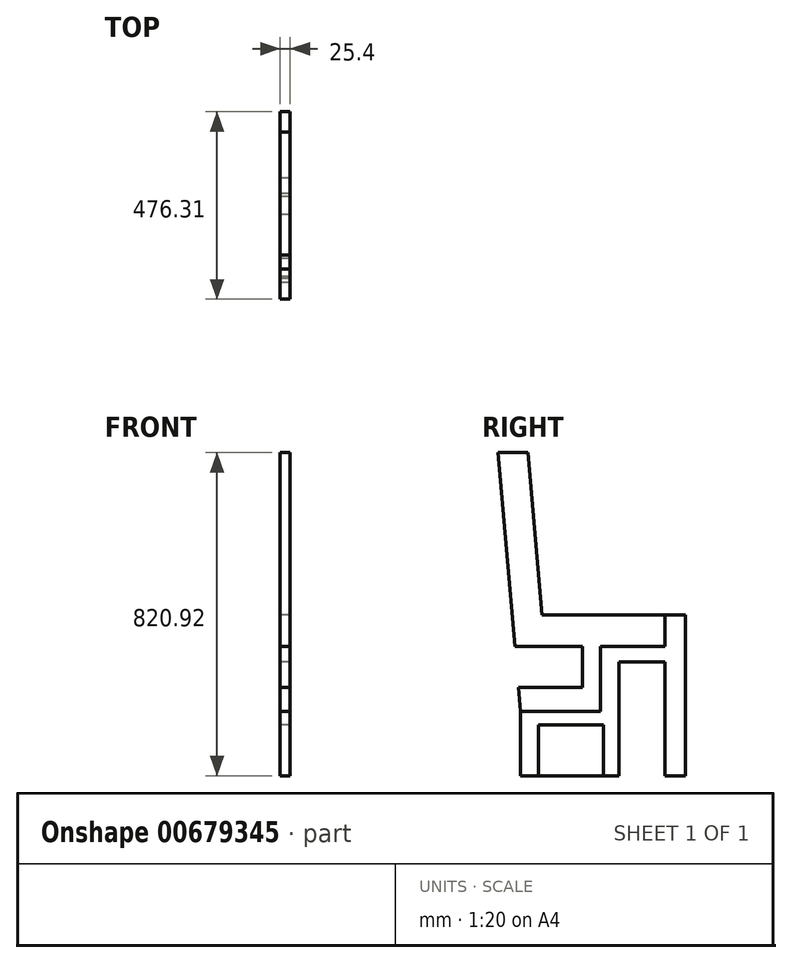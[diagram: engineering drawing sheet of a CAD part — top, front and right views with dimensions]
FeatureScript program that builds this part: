
annotation { "Feature Type Name" : "Feature", "Feature Type Description" : "" }
export const myFeature = defineFeature(function(context is Context, id is Id, definition is map)
    precondition{}
    {
        {
            var Q0;
            Q0=qCreatedBy(makeId("Right.planeOp"),FACE);
            var sketch = newSketch(context, id + "F0", { "sketchPlane" : qUnion([Q0])});
            skLineSegment(sketch, "E0", {"start": v(0.44, -2.35) * mm, "end": v(0.44, 162.75) * mm});
            skLineSegment(sketch, "E1", {"start": v(203.64, 162.75) * mm, "end": v(0.44, 162.75) * mm});
            skLineSegment(sketch, "E2", {"start": v(203.64, 162.75) * mm, "end": v(203.64, 327.85) * mm});
            skLineSegment(sketch, "E3", {"start": v(188.63, 327.85) * mm, "end": v(367.45, 327.85) * mm});
            skLineSegment(sketch, "E4", {"start": v(612.73, 408.06) * mm, "end": v(612.73, 0) * mm, "construction": true});
            skLineSegment(sketch, "E5", {"start": v(14.39, 162.75) * mm, "end": v(-951.19, 162.75) * mm, "construction": true});
            skLineSegment(sketch, "E6", {"start": v(406.4, 0) * mm, "end": v(-5.65, -0.28) * mm});
            skLineSegment(sketch, "E7", {"start": v(612.73, 0) * mm, "end": v(406.4, 0) * mm, "construction": true});
            skLineSegment(sketch, "E8", {"start": v(419.19, 408.06) * mm, "end": v(55.18, 408.06) * mm});
            skLineSegment(sketch, "E9", {"start": v(-21.15, 409.46) * mm, "end": v(0.44, 162.75) * mm});
            skLineSegment(sketch, "E10", {"start": v(419.19, 408.06) * mm, "end": v(612.73, 408.06) * mm, "construction": true});
            skLineSegment(sketch, "E11", {"start": v(-21.15, 409.46) * mm, "end": v(-57.12, 820.64) * mm});
            skLineSegment(sketch, "E12", {"start": v(-26.1, 162.75) * mm, "end": v(14.39, 162.75) * mm});
            skLineSegment(sketch, "E13", {"start": v(400.75, 0) * mm, "end": v(419.19, 0) * mm});
            skLineSegment(sketch, "E14", {"start": v(19.09, 820.64) * mm, "end": v(55.18, 408.06) * mm});
            skLineSegment(sketch, "E15", {"start": v(419.19, 408.06) * mm, "end": v(419.19, 0) * mm});
            skLineSegment(sketch, "E16.top", {"start": v(46.13, 224.39) * mm, "end": v(157.66, 224.39) * mm});
            skLineSegment(sketch, "E16.right", {"start": v(157.66, 224.39) * mm, "end": v(157.66, 328.78) * mm});
            skLineSegment(sketch, "E17.top", {"start": v(250.8, 288.85) * mm, "end": v(367.45, 288.85) * mm});
            skLineSegment(sketch, "E17.left", {"start": v(250.8, -4.98) * mm, "end": v(250.8, 288.85) * mm});
            skLineSegment(sketch, "E18.bottom", {"start": v(46.76, -0.25) * mm, "end": v(211.3, -0.25) * mm});
            skLineSegment(sketch, "E18.top", {"start": v(46.76, 128.62) * mm, "end": v(211.3, 128.62) * mm});
            skLineSegment(sketch, "E18.left", {"start": v(46.76, -0.25) * mm, "end": v(46.76, 128.62) * mm});
            skLineSegment(sketch, "E18.right", {"start": v(211.3, -0.25) * mm, "end": v(211.3, 128.62) * mm});
            skLineSegment(sketch, "E19", {"start": v(367.45, 327.85) * mm, "end": v(367.45, 414.2) * mm});
            skLineSegment(sketch, "E20", {"start": v(-57.12, 820.64) * mm, "end": v(19.09, 820.64) * mm});
            skLineSegment(sketch, "E21", {"start": v(367.45, 327.85) * mm, "end": v(419.19, 328.24) * mm});
            skLineSegment(sketch, "E22", {"start": v(419.19, 328.24) * mm, "end": v(419.19, -110.49) * mm});
            skLineSegment(sketch, "E23", {"start": v(367.45, 327.85) * mm, "end": v(367.45, -70.12) * mm});
            skLineSegment(sketch, "E24", {"start": v(211.3, 128.62) * mm, "end": v(250.8, 128.62) * mm});
            skLineSegment(sketch, "E25", {"start": v(46.13, 224.39) * mm, "end": v(32.73, 377.58) * mm});
            skLineSegment(sketch, "E26", {"start": v(157.66, 356.28) * mm, "end": v(157.66, 224.39) * mm});
            skLineSegment(sketch, "E27", {"start": v(33.9, 29.15) * mm, "end": v(367.45, 29.15) * mm});
            skLineSegment(sketch, "E28", {"start": v(157.66, 328.78) * mm, "end": v(-36.96, 328.78) * mm});
            skLineSegment(sketch, "E29", {"start": v(46.13, 224.39) * mm, "end": v(-43.71, 224.39) * mm});
            skSolve(sketch);
        }
        {
            var Q0;
            {var subQ0=sQuery(id+"F0.wireOp",EDGE,"E11");Q0=makeQuery(id+"F0.imprint","IMPRINT",FACE,{"disambiguationData":[TD([[makeQuery(id+"F0.imprint","IMPRINT",EDGE,{"derivedFrom":subQ0}),-1.0]])]});}
            var Q1;
            Q1=makeQuery(id+"F0.imprint","IMPRINT",FACE,{"disambiguationData":[TD([[makeQuery(id+"F0.imprint","IMPRINT",EDGE,{"derivedFrom":sQuery(id+"F0.wireOp",EDGE,"E1")}),-1.0]])]});
            var Q2;
            {var subQ0=sQuery(id+"F0.wireOp",EDGE,"E19");var subQ5=sQuery(id+"F0.wireOp",EDGE,"E8");var subQ6=makeQuery(id+"F0.imprint","INTERSECT",VERTEX,{"derivedFrom":[subQ5,subQ0]});Q2=makeQuery(id+"F0.imprint","IMPRINT",FACE,{"disambiguationData":[TD([[makeQuery(id+"F0.imprint","IMPRINT",EDGE,{"disambiguationData":[TD([[subQ6,-1.0]])],"derivedFrom":subQ5}),1.0]])]});}
            var Q3;
            {var subQ0=sQuery(id+"F0.wireOp",EDGE,"UJc8SRw5-JCp4-3w58-zdoM-WuLl9uJl6UIW");Q3=makeQuery(id+"F0.imprint","IMPRINT",FACE,{"disambiguationData":[TD([[makeQuery(id+"F0.imprint","IMPRINT",EDGE,{"derivedFrom":subQ0}),-1.0]])]});}
            var Q4;
            {var subQ0=sQuery(id+"F0.wireOp",EDGE,"a74wy1ss-w96l-n5P1-hgLf-OixQSZHb7zzw");Q4=makeQuery(id+"F0.imprint","IMPRINT",FACE,{"disambiguationData":[TD([[makeQuery(id+"F0.imprint","IMPRINT",EDGE,{"derivedFrom":subQ0}),1.0]])]});}
            extrude(context, id + "F1", {"entities" : qUnion([Q0, Q1, Q2, Q3, Q4]), "depth" : 25.4 * mm, "offsetDistance" : 25.4 * mm});
        }
        {
            var Q0;
            {var subQ0=sQuery(id+"F0.wireOp",EDGE,"E17.top");var subQ1=sQuery(id+"F0.wireOp",EDGE,"oAci7Kaw-5Hkm-9jKa-Rgxa-tkB4P00vJvvU");var subQ2=makeQuery(id+"F0.imprint","INTERSECT",VERTEX,{"derivedFrom":[subQ1,subQ0]});Q0=makeQuery(id+"F0.imprint","IMPRINT",FACE,{"disambiguationData":[TD([[makeQuery(id+"F0.imprint","IMPRINT",EDGE,{"disambiguationData":[TD([[subQ2,-1.0]])],"derivedFrom":subQ1}),-1.0]])]});}
            var Q1;
            {var subQ0=sQuery(id+"F0.wireOp",EDGE,"oAci7Kaw-5Hkm-9jKa-Rgxa-tkB4P00vJvvU");var subQ5=sQuery(id+"F0.wireOp",EDGE,"E17.top");var subQ7=makeQuery(id+"F0.imprint","INTERSECT",VERTEX,{"derivedFrom":[subQ0,subQ5]});Q1=makeQuery(id+"F0.imprint","IMPRINT",FACE,{"disambiguationData":[TD([[makeQuery(id+"F0.imprint","IMPRINT",EDGE,{"disambiguationData":[TD([[subQ7,1.0]])],"derivedFrom":subQ5}),1.0]])]});}
            var Q2;
            {var subQ1=sQuery(id+"F0.wireOp",EDGE,"E8");var subQ3=sQuery(id+"F0.wireOp",EDGE,"E19");var subQ4=makeQuery(id+"F0.imprint","INTERSECT",VERTEX,{"derivedFrom":[subQ1,subQ3]});Q2=makeQuery(id+"F0.imprint","IMPRINT",FACE,{"disambiguationData":[TD([[makeQuery(id+"F0.imprint","IMPRINT",EDGE,{"disambiguationData":[TD([[subQ4,1.0]])],"derivedFrom":subQ1}),1.0]])]});}
            var Q3;
            {var subQ1=sQuery(id+"F0.wireOp",EDGE,"E15");var subQ3=sQuery(id+"F0.wireOp",EDGE,"E21");var subQ4=makeQuery(id+"F0.imprint","INTERSECT",VERTEX,{"derivedFrom":[subQ1,subQ3]});Q3=makeQuery(id+"F0.imprint","IMPRINT",FACE,{"disambiguationData":[TD([[makeQuery(id+"F0.imprint","IMPRINT",EDGE,{"disambiguationData":[TD([[subQ4,1.0]])],"derivedFrom":subQ3}),1.0]])]});}
            var Q4;
            {var subQ1=sQuery(id+"F0.wireOp",EDGE,"E21");Q4=makeQuery(id+"F0.imprint","IMPRINT",FACE,{"disambiguationData":[TD([[makeQuery(id+"F0.imprint","IMPRINT",EDGE,{"derivedFrom":subQ1}),-1.0]])]});}
            var Q5;
            {var subQ0=sQuery(id+"F0.wireOp",EDGE,"E18.bottom");Q5=makeQuery(id+"F0.imprint","IMPRINT",FACE,{"disambiguationData":[TD([[makeQuery(id+"F0.imprint","IMPRINT",EDGE,{"derivedFrom":subQ0}),1.0]])]});}
            var Q6;
            {var subQ0=sQuery(id+"F0.wireOp",EDGE,"E24");Q6=makeQuery(id+"F0.imprint","IMPRINT",FACE,{"disambiguationData":[TD([[makeQuery(id+"F0.imprint","IMPRINT",EDGE,{"derivedFrom":subQ0}),-1.0]])]});}
            var Q7;
            {var subQ0=sQuery(id+"F0.wireOp",EDGE,"E17.left");var subQ1=sQuery(id+"F0.wireOp",EDGE,"E6");var subQ2=makeQuery(id+"F0.imprint","INTERSECT",VERTEX,{"derivedFrom":[subQ1,subQ0]});Q7=makeQuery(id+"F0.imprint","IMPRINT",FACE,{"disambiguationData":[TD([[makeQuery(id+"F0.imprint","IMPRINT",EDGE,{"disambiguationData":[TD([[subQ2,-1.0]])],"derivedFrom":subQ1}),-1.0]])]});}
            extrude(context, id + "F2", {"entities" : qUnion([Q0, Q1, Q2, Q3, Q4, Q5, Q6, Q7]), "depth" : 25.4 * mm, "offsetDistance" : 25.4 * mm});
        }
    });
